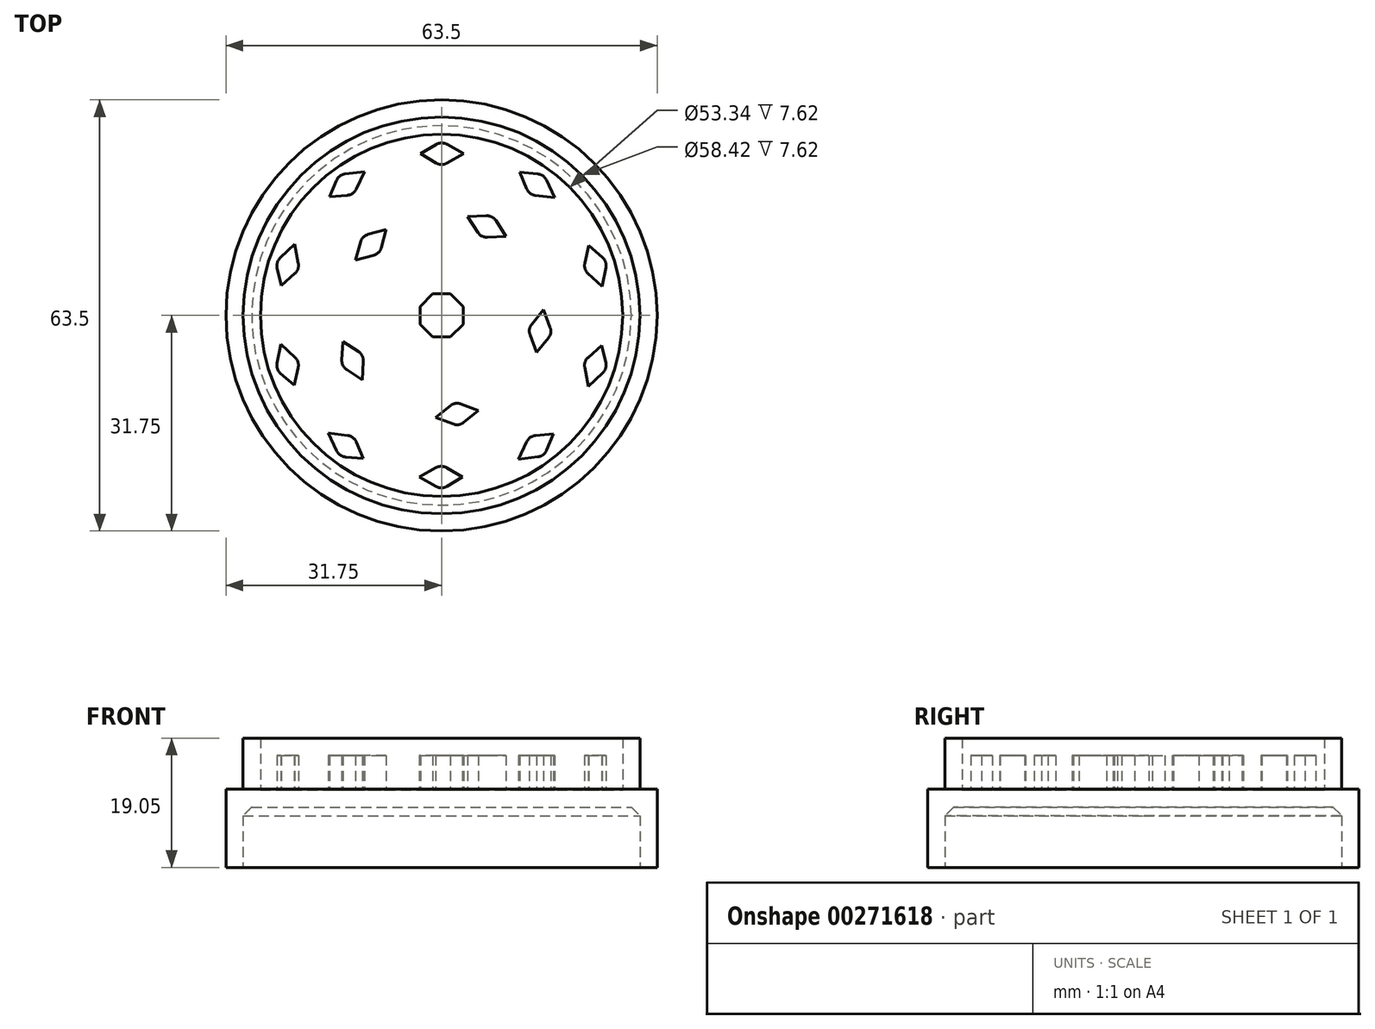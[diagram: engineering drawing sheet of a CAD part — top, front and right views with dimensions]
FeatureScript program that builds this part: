
annotation { "Feature Type Name" : "Feature", "Feature Type Description" : "" }
export const myFeature = defineFeature(function(context is Context, id is Id, definition is map)
    precondition{}
    {
        {
            var Q0;
            Q0=qCreatedBy(makeId("Front.planeOp"),FACE);
            var sketch = newSketch(context, id + "F0", { "sketchPlane" : qUnion([Q0])});
            skLineSegment(sketch, "E0", {"start": v(0, 0) * mm, "end": v(0, 32.12) * mm, "construction": true});
            skLineSegment(sketch, "E1", {"start": v(0, 0) * mm, "end": v(29.2, 0) * mm});
            skLineSegment(sketch, "E2", {"start": v(29.21, 10.16) * mm, "end": v(26.67, 10.16) * mm});
            skLineSegment(sketch, "E3", {"start": v(26.67, 10.16) * mm, "end": v(26.67, 2.54) * mm});
            skLineSegment(sketch, "E4", {"start": v(26.67, 2.54) * mm, "end": v(0, 2.54) * mm});
            skLineSegment(sketch, "E5", {"start": v(0, 2.54) * mm, "end": v(0, 0) * mm});
            skLineSegment(sketch, "E6.trimOffspring", {"start": v(29.21, 2.63) * mm, "end": v(29.21, 10.16) * mm});
            skLineSegment(sketch, "E7", {"start": v(29.21, 2.63) * mm, "end": v(31.75, 2.63) * mm});
            skLineSegment(sketch, "E8", {"start": v(31.75, 2.63) * mm, "end": v(31.75, -8.89) * mm});
            skLineSegment(sketch, "E9", {"start": v(31.75, -8.89) * mm, "end": v(29.21, -8.89) * mm});
            skLineSegment(sketch, "E10", {"start": v(29.21, -8.89) * mm, "end": v(29.21, 0) * mm});
            skSolve(sketch);
        }
        {
            var Q0;
            Q0=qSketchRegion(id+"F0",true);
            var Q1;
            Q1=sQuery(id+"F0.wireOp",EDGE,"E0");
            revolve(context, id + "F1", {"entities" : qUnion([Q0]), "axis" : qUnion([Q1]), "revolveType" : RevolveType.FULL});
        }
        {
            var Q0;
            Q0=qCreatedBy(makeId("Top.planeOp"),FACE);
            var sketch = newSketch(context, id + "F2", { "sketchPlane" : qUnion([Q0])});
            skLineSegment(sketch, "E11", {"start": v(-1.32, 3.18) * mm, "end": v(1.32, 3.18) * mm});
            skLineSegment(sketch, "E12", {"start": v(3.18, 1.32) * mm, "end": v(3.18, -1.32) * mm});
            skLineSegment(sketch, "E13", {"start": v(1.32, -3.18) * mm, "end": v(-1.32, -3.18) * mm});
            skLineSegment(sketch, "E14", {"start": v(-3.18, -1.32) * mm, "end": v(-3.18, 1.32) * mm});
            skLineSegment(sketch, "E15", {"start": v(-1.32, 3.18) * mm, "end": v(-3.18, 1.32) * mm});
            skLineSegment(sketch, "E16", {"start": v(-3.18, -1.32) * mm, "end": v(-1.32, -3.18) * mm});
            skLineSegment(sketch, "E17", {"start": v(1.32, -3.17) * mm, "end": v(3.17, -1.32) * mm});
            skLineSegment(sketch, "E18", {"start": v(3.18, 1.32) * mm, "end": v(1.32, 3.17) * mm});
            skCircle(sketch, "E19", {"center": v(0, 0) * mm, "radius": 25.4 * mm, "construction": true});
            skLineSegment(sketch, "E20", {"start": v(-0.82, 25.17) * mm, "end": v(-3.08, 23.81) * mm});
            skLineSegment(sketch, "E21", {"start": v(-3.08, 23.81) * mm, "end": v(-0.8, 22.45) * mm});
            skLineSegment(sketch, "E22", {"start": v(0.79, 22.43) * mm, "end": v(3.27, 23.81) * mm});
            skLineSegment(sketch, "E23", {"start": v(3.27, 23.81) * mm, "end": v(0.77, 25.2) * mm});
            skArc(sketch, "E24.filletArc", {"start": v(0.77, 25.2) * mm, "mid": v(-0.03, 25.4) * mm, "end": v(-0.82, 25.17) * mm});
            skArc(sketch, "E25.filletArc", {"start": v(-0.8, 22.45) * mm, "mid": v(-0.01, 22.23) * mm, "end": v(0.79, 22.43) * mm});
            skLineSegment(sketch, "E26", {"start": v(-1.19, 22.23) * mm, "end": v(1.83, 22.23) * mm, "construction": true});
            skLineSegment(sketch, "E27", {"start": v(-1.91, 25.4) * mm, "end": v(1.92, 25.4) * mm, "construction": true});
            skLineSegment(sketch, "E28.1.0", {"start": v(-11.35, 21.19) * mm, "end": v(-14.2, 20.84) * mm});
            skLineSegment(sketch, "E28.1.1", {"start": v(-15.46, 19.89) * mm, "end": v(-16.49, 17.46) * mm});
            skArc(sketch, "E28.1.2", {"start": v(-14.2, 20.84) * mm, "mid": v(-14.95, 20.53) * mm, "end": v(-15.46, 19.89) * mm});
            skLineSegment(sketch, "E28.1.3", {"start": v(-16.49, 17.46) * mm, "end": v(-13.85, 17.7) * mm});
            skArc(sketch, "E28.1.4", {"start": v(-13.85, 17.7) * mm, "mid": v(-13.07, 17.97) * mm, "end": v(-12.55, 18.6) * mm});
            skLineSegment(sketch, "E28.1.5", {"start": v(-12.55, 18.6) * mm, "end": v(-11.35, 21.19) * mm});
            skLineSegment(sketch, "E28.2.0", {"start": v(-21.64, 10.47) * mm, "end": v(-23.73, 8.52) * mm});
            skLineSegment(sketch, "E28.2.1", {"start": v(-24.2, 7) * mm, "end": v(-23.6, 4.43) * mm});
            skArc(sketch, "E28.2.2", {"start": v(-23.73, 8.52) * mm, "mid": v(-24.17, 7.82) * mm, "end": v(-24.2, 7) * mm});
            skLineSegment(sketch, "E28.2.3", {"start": v(-23.6, 4.43) * mm, "end": v(-21.6, 6.17) * mm});
            skArc(sketch, "E28.2.4", {"start": v(-21.6, 6.17) * mm, "mid": v(-21.14, 6.86) * mm, "end": v(-21.09, 7.68) * mm});
            skLineSegment(sketch, "E28.2.5", {"start": v(-21.09, 7.68) * mm, "end": v(-21.64, 10.47) * mm});
            skLineSegment(sketch, "E28.3.0", {"start": v(-23.66, -4.25) * mm, "end": v(-24.2, -7.06) * mm});
            skLineSegment(sketch, "E28.3.1", {"start": v(-23.69, -8.56) * mm, "end": v(-21.7, -10.29) * mm});
            skArc(sketch, "E28.3.2", {"start": v(-24.2, -7.06) * mm, "mid": v(-24.15, -7.88) * mm, "end": v(-23.69, -8.56) * mm});
            skLineSegment(sketch, "E28.3.3", {"start": v(-21.7, -10.29) * mm, "end": v(-21.1, -7.7) * mm});
            skArc(sketch, "E28.3.4", {"start": v(-21.1, -7.7) * mm, "mid": v(-21.13, -6.88) * mm, "end": v(-21.57, -6.18) * mm});
            skLineSegment(sketch, "E28.3.5", {"start": v(-21.57, -6.18) * mm, "end": v(-23.66, -4.25) * mm});
            skLineSegment(sketch, "E28.4.0", {"start": v(-16.64, -17.34) * mm, "end": v(-15.44, -19.94) * mm});
            skLineSegment(sketch, "E28.4.1", {"start": v(-14.14, -20.85) * mm, "end": v(-11.5, -21.08) * mm});
            skArc(sketch, "E28.4.2", {"start": v(-15.44, -19.94) * mm, "mid": v(-14.9, -20.57) * mm, "end": v(-14.14, -20.85) * mm});
            skLineSegment(sketch, "E28.4.3", {"start": v(-11.5, -21.08) * mm, "end": v(-12.55, -18.64) * mm});
            skArc(sketch, "E28.4.4", {"start": v(-12.55, -18.64) * mm, "mid": v(-13.05, -17.99) * mm, "end": v(-13.82, -17.68) * mm});
            skLineSegment(sketch, "E28.4.5", {"start": v(-13.82, -17.68) * mm, "end": v(-16.64, -17.34) * mm});
            skLineSegment(sketch, "E28.5.0", {"start": v(-3.27, -23.81) * mm, "end": v(-0.77, -25.2) * mm});
            skLineSegment(sketch, "E28.5.1", {"start": v(0.82, -25.17) * mm, "end": v(3.08, -23.81) * mm});
            skArc(sketch, "E28.5.2", {"start": v(-0.77, -25.2) * mm, "mid": v(0.03, -25.4) * mm, "end": v(0.82, -25.17) * mm});
            skLineSegment(sketch, "E28.5.3", {"start": v(3.08, -23.81) * mm, "end": v(0.8, -22.45) * mm});
            skArc(sketch, "E28.5.4", {"start": v(0.8, -22.45) * mm, "mid": v(0.01, -22.23) * mm, "end": v(-0.79, -22.43) * mm});
            skLineSegment(sketch, "E28.5.5", {"start": v(-0.79, -22.43) * mm, "end": v(-3.27, -23.81) * mm});
            skLineSegment(sketch, "E28.6.0", {"start": v(11.35, -21.19) * mm, "end": v(14.2, -20.84) * mm});
            skLineSegment(sketch, "E28.6.1", {"start": v(15.46, -19.89) * mm, "end": v(16.49, -17.46) * mm});
            skArc(sketch, "E28.6.2", {"start": v(14.2, -20.84) * mm, "mid": v(14.95, -20.53) * mm, "end": v(15.46, -19.89) * mm});
            skLineSegment(sketch, "E28.6.3", {"start": v(16.49, -17.46) * mm, "end": v(13.85, -17.7) * mm});
            skArc(sketch, "E28.6.4", {"start": v(13.85, -17.7) * mm, "mid": v(13.07, -17.97) * mm, "end": v(12.55, -18.6) * mm});
            skLineSegment(sketch, "E28.6.5", {"start": v(12.55, -18.6) * mm, "end": v(11.35, -21.19) * mm});
            skLineSegment(sketch, "E28.7.0", {"start": v(21.64, -10.47) * mm, "end": v(23.73, -8.52) * mm});
            skLineSegment(sketch, "E28.7.1", {"start": v(24.2, -7) * mm, "end": v(23.6, -4.43) * mm});
            skArc(sketch, "E28.7.2", {"start": v(23.73, -8.52) * mm, "mid": v(24.17, -7.82) * mm, "end": v(24.2, -7) * mm});
            skLineSegment(sketch, "E28.7.3", {"start": v(23.6, -4.43) * mm, "end": v(21.6, -6.17) * mm});
            skArc(sketch, "E28.7.4", {"start": v(21.6, -6.17) * mm, "mid": v(21.14, -6.86) * mm, "end": v(21.09, -7.68) * mm});
            skLineSegment(sketch, "E28.7.5", {"start": v(21.09, -7.68) * mm, "end": v(21.64, -10.47) * mm});
            skLineSegment(sketch, "E28.8.0", {"start": v(23.66, 4.25) * mm, "end": v(24.2, 7.06) * mm});
            skLineSegment(sketch, "E28.8.1", {"start": v(23.69, 8.56) * mm, "end": v(21.7, 10.29) * mm});
            skArc(sketch, "E28.8.2", {"start": v(24.2, 7.06) * mm, "mid": v(24.15, 7.88) * mm, "end": v(23.69, 8.56) * mm});
            skLineSegment(sketch, "E28.8.3", {"start": v(21.7, 10.29) * mm, "end": v(21.1, 7.7) * mm});
            skArc(sketch, "E28.8.4", {"start": v(21.1, 7.7) * mm, "mid": v(21.13, 6.88) * mm, "end": v(21.57, 6.18) * mm});
            skLineSegment(sketch, "E28.8.5", {"start": v(21.57, 6.18) * mm, "end": v(23.66, 4.25) * mm});
            skLineSegment(sketch, "E28.9.0", {"start": v(16.64, 17.34) * mm, "end": v(15.44, 19.94) * mm});
            skLineSegment(sketch, "E28.9.1", {"start": v(14.14, 20.85) * mm, "end": v(11.5, 21.08) * mm});
            skArc(sketch, "E28.9.2", {"start": v(15.44, 19.94) * mm, "mid": v(14.9, 20.57) * mm, "end": v(14.14, 20.85) * mm});
            skLineSegment(sketch, "E28.9.3", {"start": v(11.5, 21.08) * mm, "end": v(12.55, 18.64) * mm});
            skArc(sketch, "E28.9.4", {"start": v(12.55, 18.64) * mm, "mid": v(13.05, 17.99) * mm, "end": v(13.82, 17.68) * mm});
            skLineSegment(sketch, "E28.9.5", {"start": v(13.82, 17.68) * mm, "end": v(16.64, 17.34) * mm});
            skLineSegment(sketch, "E29", {"start": v(-8.15, 12.64) * mm, "end": v(-12.64, 8.15) * mm, "construction": true});
            skLineSegment(sketch, "E30", {"start": v(-10.4, 10.4) * mm, "end": v(0, 0) * mm, "construction": true});
            skLineSegment(sketch, "E31", {"start": v(-12.64, 8.15) * mm, "end": v(-9.98, 8.86) * mm});
            skLineSegment(sketch, "E32", {"start": v(-8.86, 9.98) * mm, "end": v(-8.15, 12.64) * mm});
            skLineSegment(sketch, "E33", {"start": v(-8.15, 12.64) * mm, "end": v(-10.8, 11.93) * mm});
            skLineSegment(sketch, "E34", {"start": v(-11.93, 10.8) * mm, "end": v(-12.64, 8.15) * mm});
            skArc(sketch, "E35", {"start": v(-10.8, 11.93) * mm, "mid": v(-11.52, 11.52) * mm, "end": v(-11.93, 10.8) * mm});
            skArc(sketch, "E36", {"start": v(-9.98, 8.86) * mm, "mid": v(-9.27, 9.27) * mm, "end": v(-8.86, 9.98) * mm});
            skLineSegment(sketch, "E37.1.0", {"start": v(-14.54, -3.84) * mm, "end": v(-14.68, -6.6) * mm});
            skLineSegment(sketch, "E37.1.1", {"start": v(-12.23, -5.34) * mm, "end": v(-14.54, -3.84) * mm});
            skArc(sketch, "E37.1.2", {"start": v(-11.51, -6.76) * mm, "mid": v(-11.68, -5.95) * mm, "end": v(-12.23, -5.34) * mm});
            skLineSegment(sketch, "E37.1.3", {"start": v(-11.66, -9.5) * mm, "end": v(-11.51, -6.76) * mm});
            skLineSegment(sketch, "E37.1.4", {"start": v(-13.96, -8) * mm, "end": v(-11.66, -9.5) * mm});
            skArc(sketch, "E37.1.5", {"start": v(-14.68, -6.6) * mm, "mid": v(-14.51, -7.4) * mm, "end": v(-13.96, -8) * mm});
            skLineSegment(sketch, "E37.2.0", {"start": v(-0.84, -15.02) * mm, "end": v(1.73, -16) * mm});
            skLineSegment(sketch, "E37.2.1", {"start": v(1.3, -13.28) * mm, "end": v(-0.84, -15.02) * mm});
            skArc(sketch, "E37.2.2", {"start": v(2.87, -13.04) * mm, "mid": v(2.05, -12.95) * mm, "end": v(1.3, -13.28) * mm});
            skLineSegment(sketch, "E37.2.3", {"start": v(5.44, -14.02) * mm, "end": v(2.87, -13.04) * mm});
            skLineSegment(sketch, "E37.2.4", {"start": v(3.3, -15.75) * mm, "end": v(5.44, -14.02) * mm});
            skArc(sketch, "E37.2.5", {"start": v(1.73, -16) * mm, "mid": v(2.55, -16.09) * mm, "end": v(3.3, -15.75) * mm});
            skLineSegment(sketch, "E37.3.0", {"start": v(14.02, -5.44) * mm, "end": v(15.75, -3.3) * mm});
            skLineSegment(sketch, "E37.3.1", {"start": v(13.04, -2.87) * mm, "end": v(14.02, -5.44) * mm});
            skArc(sketch, "E37.3.2", {"start": v(13.28, -1.3) * mm, "mid": v(12.95, -2.05) * mm, "end": v(13.04, -2.87) * mm});
            skLineSegment(sketch, "E37.3.3", {"start": v(15.02, 0.84) * mm, "end": v(13.28, -1.3) * mm});
            skLineSegment(sketch, "E37.3.4", {"start": v(16, -1.73) * mm, "end": v(15.02, 0.84) * mm});
            skArc(sketch, "E37.3.5", {"start": v(15.75, -3.3) * mm, "mid": v(16.09, -2.55) * mm, "end": v(16, -1.73) * mm});
            skLineSegment(sketch, "E37.4.0", {"start": v(9.5, 11.66) * mm, "end": v(8, 13.96) * mm});
            skLineSegment(sketch, "E37.4.1", {"start": v(6.76, 11.51) * mm, "end": v(9.5, 11.66) * mm});
            skArc(sketch, "E37.4.2", {"start": v(5.34, 12.23) * mm, "mid": v(5.95, 11.68) * mm, "end": v(6.76, 11.51) * mm});
            skLineSegment(sketch, "E37.4.3", {"start": v(3.84, 14.54) * mm, "end": v(5.34, 12.23) * mm});
            skLineSegment(sketch, "E37.4.4", {"start": v(6.6, 14.68) * mm, "end": v(3.84, 14.54) * mm});
            skArc(sketch, "E37.4.5", {"start": v(8, 13.96) * mm, "mid": v(7.4, 14.51) * mm, "end": v(6.6, 14.68) * mm});
            skSolve(sketch);
        }
        {
            var Q0;
            Q0=qSketchRegion(id+"F2",true);
            extrude(context, id + "F3", {"entities" : qUnion([Q0]), "operationType" : NewBodyOperationType.ADD, "depth" : 7.62 * mm});
        }
        {
            var Q0;
            Q0=qSketchRegion(id+"F2",true);
            extrude(context, id + "F4", {"entities" : qUnion([Q0]), "operationType" : NewBodyOperationType.ADD, "depth" : 7.62 * mm});
        }
        {
            var Q0;
            Q0=makeQuery(id+"F1.opRevolve","SWEPT_EDGE",EDGE,{"disambiguationData":[OSD([sQuery(id+"F0.wireOp",EDGE,"E1"),sQuery(id+"F0.wireOp",EDGE,"MRAsCIAv-yq4A-nb9H-V6nn-eikL1hEkFUVH")])]});
            chamfer(context, id + "F5", {"entities" : qUnion([Q0]), "chamferType" : ChamferType.OFFSET_ANGLE, "width" : 1.27 * mm, "oppositeDirection" : false, "angle" : 45 * degree, "tangentPropagation" : true});
        }
    });
